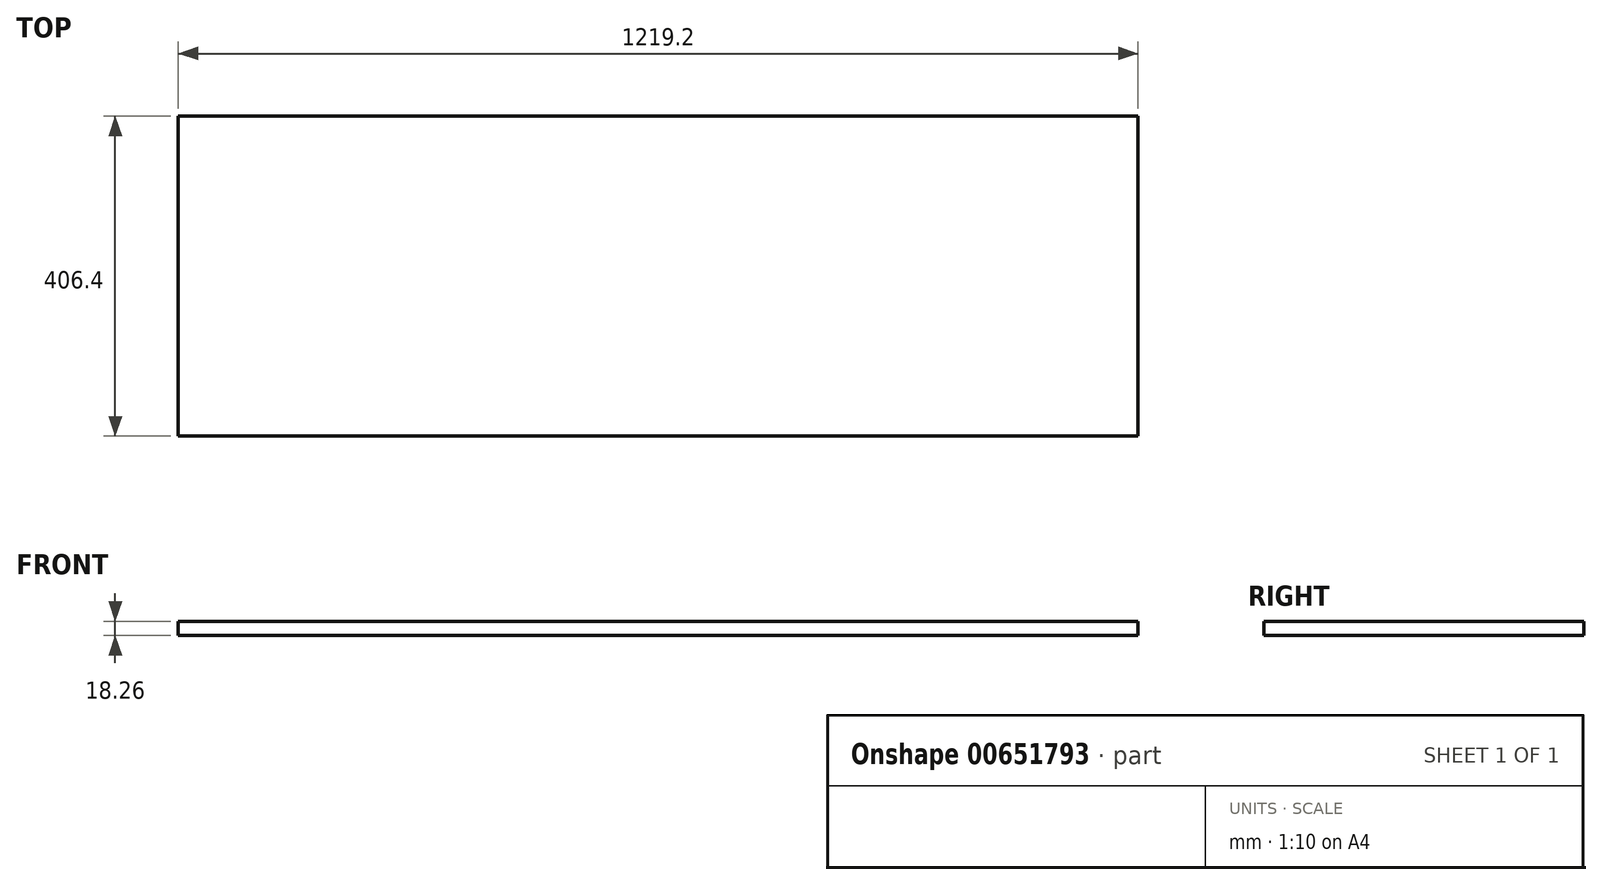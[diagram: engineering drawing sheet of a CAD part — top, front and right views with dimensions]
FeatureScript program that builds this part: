
annotation { "Feature Type Name" : "Feature", "Feature Type Description" : "" }
export const myFeature = defineFeature(function(context is Context, id is Id, definition is map)
    precondition{}
    {
        {
            var Q0;
            Q0=qCreatedBy(makeId("Top.planeOp"),FACE);
            var sketch = newSketch(context, id + "F0", { "sketchPlane" : qUnion([Q0])});
            skLineSegment(sketch, "E0.bottom", {"start": v(0, 0) * mm, "end": v(1219.2, 0) * mm});
            skLineSegment(sketch, "E0.top", {"start": v(0, 406.4) * mm, "end": v(1219.2, 406.4) * mm});
            skLineSegment(sketch, "E0.left", {"start": v(0, 0) * mm, "end": v(0, 406.4) * mm});
            skLineSegment(sketch, "E0.right", {"start": v(1219.2, 0) * mm, "end": v(1219.2, 406.4) * mm});
            skSolve(sketch);
        }
        {
            var Q0;
            Q0=makeQuery(id+"F0.imprint","IMPRINT",FACE,{"disambiguationData":[TD([[makeQuery(id+"F0.imprint","IMPRINT",EDGE,{"derivedFrom":sQuery(id+"F0.wireOp",EDGE,"E0.bottom")}),1.0]])]});
            extrude(context, id + "F1", {"entities" : qUnion([Q0]), "depth" : 18.26 * mm, "offsetDistance" : 25.4 * mm});
        }
    });
